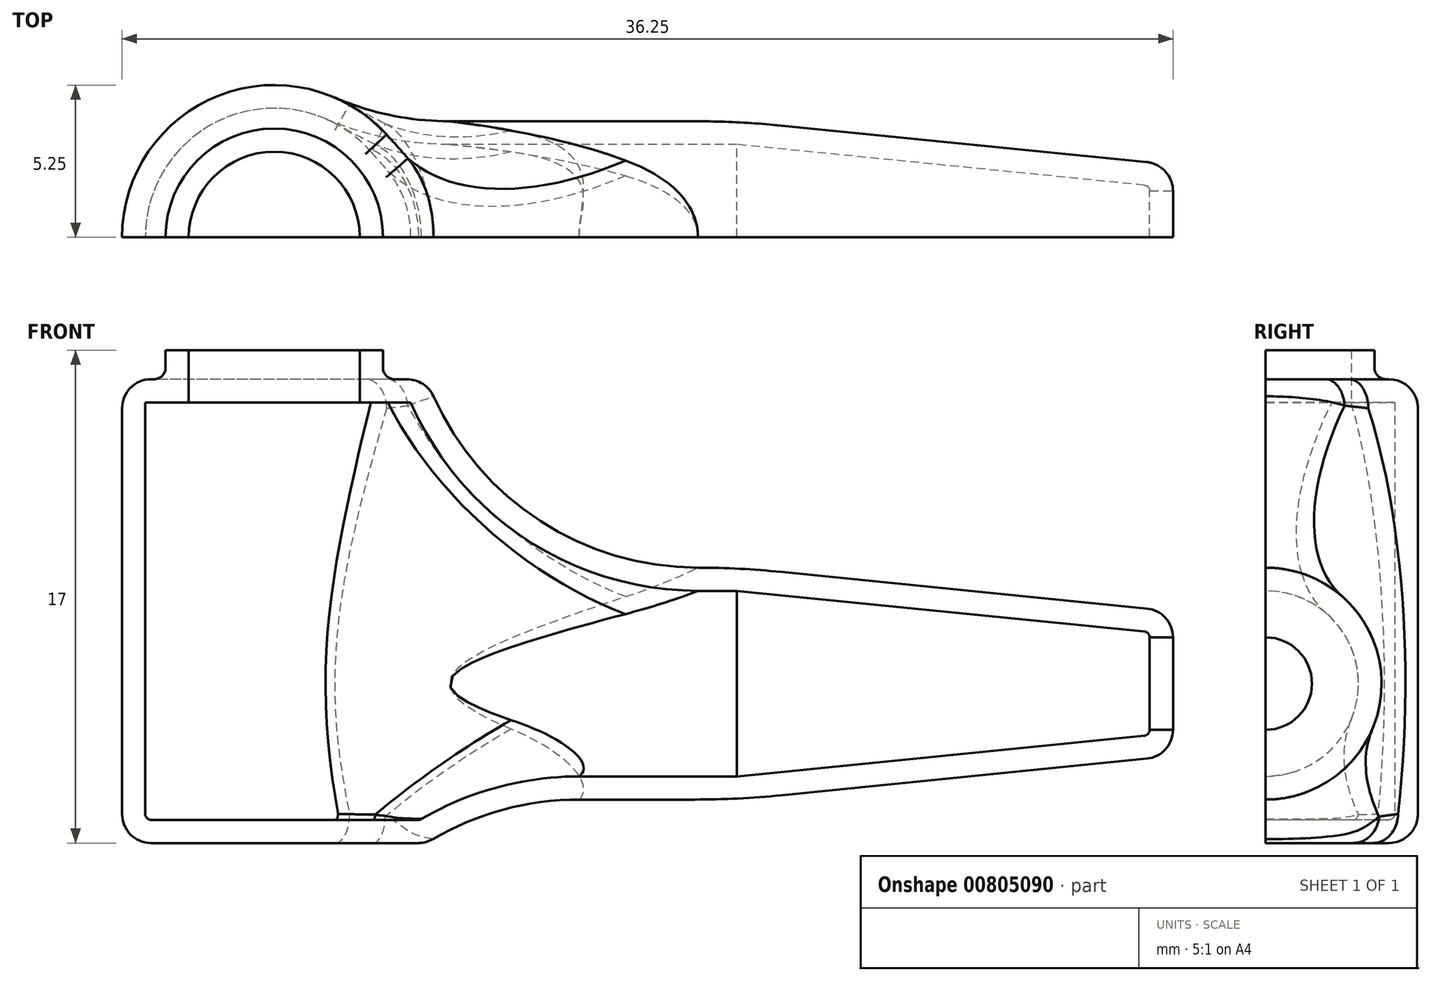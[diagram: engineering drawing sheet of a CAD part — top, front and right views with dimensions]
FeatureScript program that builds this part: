
annotation { "Feature Type Name" : "Feature", "Feature Type Description" : "" }
export const myFeature = defineFeature(function(context is Context, id is Id, definition is map)
    precondition{}
    {
        {
            var Q0;
            Q0=qCreatedBy(makeId("Top.planeOp"),FACE);
            var sketch = newSketch(context, id + "F0", { "sketchPlane" : qUnion([Q0])});
            skCircle(sketch, "E0", {"center": v(0, 0) * mm, "radius": 2.85 * mm});
            skCircle(sketch, "E1", {"center": v(0, 0) * mm, "radius": 3.75 * mm});
            skCircle(sketch, "E2", {"center": v(0, 0) * mm, "radius": 5.25 * mm});
            skSolve(sketch);
        }
        {
            var Q0;
            Q0=makeQuery(id+"F0.imprint","IMPRINT",FACE,{"disambiguationData":[TD([[makeQuery(id+"F0.imprint","IMPRINT",EDGE,{"derivedFrom":sQuery(id+"F0.wireOp",EDGE,"E0")}),-1.0]])]});
            var Q1;
            Q1=makeQuery(id+"F0.imprint","IMPRINT",FACE,{"disambiguationData":[TD([[makeQuery(id+"F0.imprint","IMPRINT",EDGE,{"derivedFrom":sQuery(id+"F0.wireOp",EDGE,"E0")}),1.0]])]});
            extrude(context, id + "F1", {"entities" : qUnion([Q0, Q1]), "depth" : 2 * mm, "offsetDistance" : 25 * mm});
        }
        {
            var Q0;
            Q0=makeQuery(id+"F0.imprint","IMPRINT",FACE,{"disambiguationData":[TD([[makeQuery(id+"F0.imprint","IMPRINT",EDGE,{"derivedFrom":sQuery(id+"F0.wireOp",EDGE,"E1")}),-1.0]])]});
            var Q1;
            Q1=makeQuery(id+"F0.imprint","IMPRINT",FACE,{"disambiguationData":[TD([[makeQuery(id+"F0.imprint","IMPRINT",EDGE,{"derivedFrom":sQuery(id+"F0.wireOp",EDGE,"E0")}),-1.0]])]});
            var Q2;
            Q2=makeQuery(id+"F0.imprint","IMPRINT",FACE,{"disambiguationData":[TD([[makeQuery(id+"F0.imprint","IMPRINT",EDGE,{"derivedFrom":sQuery(id+"F0.wireOp",EDGE,"E0")}),1.0]])]});
            extrude(context, id + "F2", {"entities" : qUnion([Q0, Q1, Q2]), "operationType" : NewBodyOperationType.ADD, "depth" : 1 * mm, "offsetDistance" : 25 * mm, "hasSecondDirection" : true, "secondDirectionOppositeDirection" : true, "secondDirectionDepth" : 15 * mm});
        }
        {
            var Q0;
            Q0=qCreatedBy(makeId("Front.planeOp"),FACE);
            var sketch = newSketch(context, id + "F3", { "sketchPlane" : qUnion([Q0])});
            skLineSegment(sketch, "E3", {"start": v(-30.45, -9.5) * mm, "end": v(21.56, -9.5) * mm, "construction": true});
            skSolve(sketch);
        }
        {
            var Q0;
            Q0=qCreatedBy(makeId("Right.planeOp"),FACE);
            var sketch = newSketch(context, id + "F4", { "sketchPlane" : qUnion([Q0])});
            skPoint(sketch, "E4", {"position": v(0, -9.5) * mm});
            skCircle(sketch, "E5", {"center": v(0, -9.5) * mm, "radius": 4 * mm});
            skSolve(sketch);
        }
        {
            var Q0;
            Q0=makeQuery(id+"F4.imprint","IMPRINT",FACE,{"disambiguationData":[TD([[makeQuery(id+"F4.imprint","IMPRINT",EDGE,{"derivedFrom":sQuery(id+"F4.wireOp",EDGE,"E5")}),1.0]])]});
            extrude(context, id + "F5", {"entities" : qUnion([Q0]), "operationType" : NewBodyOperationType.ADD, "depth" : 31 * mm, "offsetDistance" : 25 * mm});
        }
        {
            var Q0;
            Q0=makeQuery(id+"F5.opExtrude","CAP_EDGE",EDGE,{"disambiguationData":[OSD([sQuery(id+"F4.wireOp",EDGE,"E5")])],"isStart":false});
            chamfer(context, id + "F6", {"entities" : qUnion([Q0]), "chamferType" : ChamferType.TWO_OFFSETS, "width1" : 15 * mm, "oppositeDirection" : true, "width2" : 1.5 * mm, "tangentPropagation" : true});
        }
        {
            var Q0;
            Q0=makeQuery(id+"F5.boolean.opBoolean","INTERSECT",EDGE,{"derivedFrom":[makeQuery(id+"F2.opExtrude","SWEPT_FACE",FACE,{"disambiguationData":[OSD([sQuery(id+"F0.wireOp",EDGE,"E2")])]}),makeQuery(id+"F5.opExtrude","SWEPT_FACE",FACE,{"disambiguationData":[OSD([sQuery(id+"F4.wireOp",EDGE,"E5")])]})]});
            fillet(context, id + "F7", {"entities" : qUnion([Q0]), "radius" : 10 * mm, "tangentPropagation" : true, "allowEdgeOverflow" : false});
        }
        {
            var Q0;
            Q0=makeQuery(id+"F2.opExtrude","CAP_EDGE",EDGE,{"disambiguationData":[OSD([sQuery(id+"F0.wireOp",EDGE,"E2")])],"isStart":true});
            fillet(context, id + "F8", {"entities" : qUnion([Q0]), "radius" : 1 * mm, "tangentPropagation" : true, "allowEdgeOverflow" : false});
        }
        {
            var Q0;
            {var subQ0=sQuery(id+"F4.wireOp",EDGE,"E5");Q0=makeQuery(id+"F6.opChamfer","BLEND_EDGE",EDGE,{"blendedFrom":[makeQuery(id+"F5.opExtrude","CAP_EDGE",EDGE,{"disambiguationData":[OSD([subQ0])],"isStart":false}),makeQuery(id+"F5.opExtrude","CAP_FACE",FACE,{"disambiguationData":[OSD([subQ0])],"isStart":false})],"blendedInto":[makeQuery(id+"F5.opExtrude","CAP_FACE",FACE,{"disambiguationData":[OSD([subQ0])],"isStart":false})]});}
            fillet(context, id + "F9", {"entities" : qUnion([Q0]), "radius" : 1 * mm, "tangentPropagation" : true, "allowEdgeOverflow" : false});
        }
        {
            var Q0;
            Q0=makeQuery(id+"F5.opExtrude","CAP_FACE",FACE,{"disambiguationData":[OSD([sQuery(id+"F4.wireOp",EDGE,"E5")])],"isStart":false});
            var Q1;
            Q1=makeQuery(id+"F1.opExtrude","CAP_FACE",FACE,{"disambiguationData":[OSD([sQuery(id+"F0.wireOp",EDGE,"E1")])],"isStart":false});
            shell(context, id + "F10", {"entities" : qUnion([Q0, Q1]), "thickness" : 0.8 * mm});
        }
        {
            var Q0;
            Q0=qCreatedBy(makeId("Front.planeOp"),FACE);
            var sketch = newSketch(context, id + "F11", { "sketchPlane" : qUnion([Q0])});
            skLineSegment(sketch, "E6.bottom", {"start": v(-27.92, -47.67) * mm, "end": v(50.1, -47.67) * mm});
            skLineSegment(sketch, "E6.top", {"start": v(-27.92, 39.45) * mm, "end": v(50.1, 39.45) * mm});
            skLineSegment(sketch, "E6.left", {"start": v(-27.92, -47.67) * mm, "end": v(-27.92, 39.45) * mm});
            skLineSegment(sketch, "E6.right", {"start": v(50.1, -47.67) * mm, "end": v(50.1, 39.45) * mm});
            skSolve(sketch);
        }
        {
            var Q0;
            Q0=makeQuery(id+"F11.imprint","IMPRINT",FACE,{"disambiguationData":[TD([[makeQuery(id+"F11.imprint","IMPRINT",EDGE,{"derivedFrom":sQuery(id+"F11.wireOp",EDGE,"E6.bottom")}),1.0]])]});
            extrude(context, id + "F12", {"entities" : qUnion([Q0]), "depth" : 10 * mm, "offsetDistance" : 25 * mm});
        }
        {
            var Q0;
            Q0=makeQuery(id+"F12.opExtrude","SWEPT_BODY",BODY,{"disambiguationData":[OSD([sQuery(id+"F11.wireOp",EDGE,"E6.bottom"),sQuery(id+"F11.wireOp",EDGE,"E6.top"),sQuery(id+"F11.wireOp",EDGE,"E6.left"),sQuery(id+"F11.wireOp",EDGE,"E6.right")])]});
            var Q1;
            Q1=makeQuery(id+"F1.opExtrude","SWEPT_BODY",BODY,{"disambiguationData":[OSD([sQuery(id+"F0.wireOp",EDGE,"E1")])]});
            booleanBodies(context, id + "F13", {"operationType" : BooleanOperationType.SUBTRACTION, "tools" : qUnion([Q0]), "targets" : qUnion([Q1])});
        }
        {
            var Q0;
            Q0=makeQuery(id+"F2.opExtrude","CAP_EDGE",EDGE,{"disambiguationData":[OSD([sQuery(id+"F0.wireOp",EDGE,"E2")])],"isStart":false});
            fillet(context, id + "F14", {"entities" : qUnion([Q0]), "radius" : 1 * mm, "tangentPropagation" : true, "allowEdgeOverflow" : false});
        }
        {
            var Q0;
            Q0=makeQuery(id+"F2.boolean.opBoolean","INTERSECT",EDGE,{"derivedFrom":[makeQuery(id+"F1.opExtrude","SWEPT_FACE",FACE,{"disambiguationData":[OSD([sQuery(id+"F0.wireOp",EDGE,"E1")])]}),makeQuery(id+"F2.opExtrude","CAP_FACE",FACE,{"disambiguationData":[OSD([sQuery(id+"F0.wireOp",EDGE,"E2")])],"isStart":false})]});
            fillet(context, id + "F15", {"entities" : qUnion([Q0]), "radius" : 0.4 * mm, "tangentPropagation" : true, "allowEdgeOverflow" : false});
        }
        {
            var Q0;
            {var subQ0=sQuery(id+"F4.wireOp",EDGE,"E5");Q0=makeQuery(id+"F6.opChamfer","BLEND_EDGE",EDGE,{"blendedFrom":[makeQuery(id+"F5.opExtrude","CAP_EDGE",EDGE,{"disambiguationData":[OSD([subQ0])],"isStart":false}),makeQuery(id+"F5.opExtrude","SWEPT_FACE",FACE,{"disambiguationData":[OSD([subQ0])]})],"blendedInto":[makeQuery(id+"F5.opExtrude","SWEPT_FACE",FACE,{"disambiguationData":[OSD([subQ0])]})]});}
            fillet(context, id + "F16", {"entities" : qUnion([Q0]), "radius" : 30 * mm, "tangentPropagation" : true, "allowEdgeOverflow" : false});
        }
    });
